# Revit family: Thorn ALTIS GEN5 2 Modules
name_source: partatom
category: Lighting Fixtures
units: mm (PartAtom-declared; Revit-internal decimal feet)

## family parameters
Cut with Voids When Loaded = No
Host = Face
Light Source = No
Maintain Annotation Orientation = No
Part Type = Normal
Room Calculation Point = Yes
Round Connector Dimension = Use Diameter
Shared = No

## types (26) — shared parameters
Assembly Code = Pr_70_70_48_31
Connection Box Left Inside = No
Connection Box Left Outside = Yes
Connection Box Right Inside = No
Connection Box Right Outside = No
Description = Sports Floodlighting
Export Type to IFC As = IfcLightFixtureType
Gearbox = No
Initial Color Temperature = 4000 K
Lamp = LED
Luminaire Height = 574 mm  [stored 1.8832 ft]
Luminaire Length = 530 mm  [stored 1.73885 ft]
Luminaire Width = 757 mm
Manufacturer = Zumtobel Lighting
Material = Thorn-Aluminium-RAL 7043-Traffic Grey B
Power Factor = 1
SELECT ACCESSORIES = SELECT CONNECTION BOX POSITION
SELECT CONNECTION BOX POSITION = SELECT CONNECTION BOX POSITION
SELECT GEARBOX TYPE = SELECT CONNECTION BOX POSITION
SELECT MODULE PROPERTIES = SELECT MODULE PROPERTIES
Type Gearbox = Thorn ALTIS GEN5 Gearbox-Premium-class C5 with NTC : ALG5 GB 1368W 1.40A 565V 2CH DA
Type IFC Predefined Type = DIRECTIONSOURCE
URL = https://www.thornlighting.com
zero-valued in all types: Default Elevation

## per-type parameters (varying)
| type | Apparent Load | Balanced White Colour | Model | RGB Light Colours | Type Image | Wattage |
| ALG5 288L105-740 PST A6A6 ANT | 912 VA | No | 96684116 | No | TLG_ALT5_F_V2_FIFA.jpg | 912 W |
| ALG5 288L125-740 PST A6A6 ANT | 1095 VA | No | 96684115 | No | TLG_ALT5_F_V2_FIFA.jpg | 1095 W |
| ALG5 288L140-740 PST A6A6 ANT | 1225 VA | No | 96670251 | No | TLG_ALT5_F_V2_FIFA.jpg | 1225 W |
| ALG5 288L70-740 PST A6A6 ANT | 594 VA | No | 96684118 | No | TLG_ALT5_F_V2_FIFA.jpg | 594 W |
| ALG5 288L85-740 PST A6A6 ANT | 730 VA | No | 96684117 | No | TLG_ALT5_F_V2_FIFA.jpg | 730 W |
| ALG5 312L105-740 PST NBA6 ANT | 987 VA | No | 96684120 | No | TLG_ALT5_F_V2_FIFA.jpg | 987 W |
| ALG5 312L125-740 PST NBA6 ANT | 1184 VA | No | 96684119 | No | TLG_ALT5_F_V2_FIFA.jpg | 1184 W |
| ALG5 312L70-740 PST NBA6 ANT | 644 VA | No | 96684122 | No | TLG_ALT5_F_V2_FIFA.jpg | 644 W |
| ALG5 312L85-740 PST NBA6 ANT | 791 VA | No | 96684121 | No | TLG_ALT5_F_V2_FIFA.jpg | 791 W |
| ALG5 336L105-740 PST NBNB ANT | 1060 VA | No | 96684123 | No | TLG_ALT5_F_V2_FIFA.jpg | 1060 W |
| ALG5 336L125-740 PST NBNB ANT | 1272 VA | No | 96670252 | No | TLG_ALT5_F_V2_FIFA.jpg | 1272 W |
| ALG5 336L70-740 PST NBNB ANT | 691 VA | No | 96684125 | No | TLG_ALT5_F_V2_FIFA.jpg | 691 W |
| ALG5 336L85-740 PST NBNB ANT | 849 VA | No | 96684124 | No | TLG_ALT5_F_V2_FIFA.jpg | 849 W |
| ALG5 LE 288L105-740 PST A6A6 ANT | 912 VA | No | 96800079 | No | TLG_ALT5_F_V2_FIFA.jpg | 912 W |
| ALG5 LE 288L125-740 PST A6A6 ANT | 1095 VA | No | 96800078 | No | TLG_ALT5_F_V2_FIFA.jpg | 1095 W |
| ALG5 LE 288L140-740 PST A6A6 ANT | 1225 VA | No | 96800077 | No | TLG_ALT5_F_V2_FIFA.jpg | 1225 W |
| ALG5 LE 288L85-740 PST A6A6 ANT | 730 VA | No | 96800080 | No | TLG_ALT5_F_V2_FIFA.jpg | 730 W |
| ALG5 LE 312L105-740 PST NBA6 ANT | 987 VA | No | 96800082 | No | TLG_ALT5_F_V2_FIFA.jpg | 987 W |
| ALG5 LE 312L125-740 PST NBA6 ANT | 1184 VA | No | 96800081 | No | TLG_ALT5_F_V2_FIFA.jpg | 1184 W |
| ALG5 LE 312L85-740 PST NBA6 ANT | 791 VA | No | 96800083 | No | TLG_ALT5_F_V2_FIFA.jpg | 791 W |
| ALG5 LE 336L105-740 PST NBNB ANT | 1060 VA | No | 96800085 | No | TLG_ALT5_F_V2_FIFA.jpg | 1060 W |
| ALG5 LE 336L125-740 PST NBNB ANT | 1272 VA | No | 96800084 | No | TLG_ALT5_F_V2_FIFA.jpg | 1272 W |
| ALG5 LE 336L85-740 PST NBNB ANT | 849 VA | No | 96800086 | No | TLG_ALT5_F_V2_FIFA.jpg | 849 W |
| ALG5 RGBW 264L85 B PAR NB NB ANT | 681 VA | No | 96685675 | Yes | TLG_ALT5_F_V2_ANT_RGBW.jpg | 681 W |
| ALG5 BW 264L105 B PAR EWEW ANT | 825 VA | Yes | 96685679 | No | TLG_ALT5_F_V2_ANT_BW.jpg | 825 W |
| ALG5 BW 264L85 B PAR EWEW ANT | 661 VA | Yes | 96685680 | No | TLG_ALT5_F_V2_ANT_BW.jpg | 661 W |

note: [stored X ft] marks values corroborated as IEEE doubles in the binary element streams (Revit-internal decimal feet)

## geometry (parser evidence)
native form markers: Sweep x18
no freeform markers — native parametric forms only
